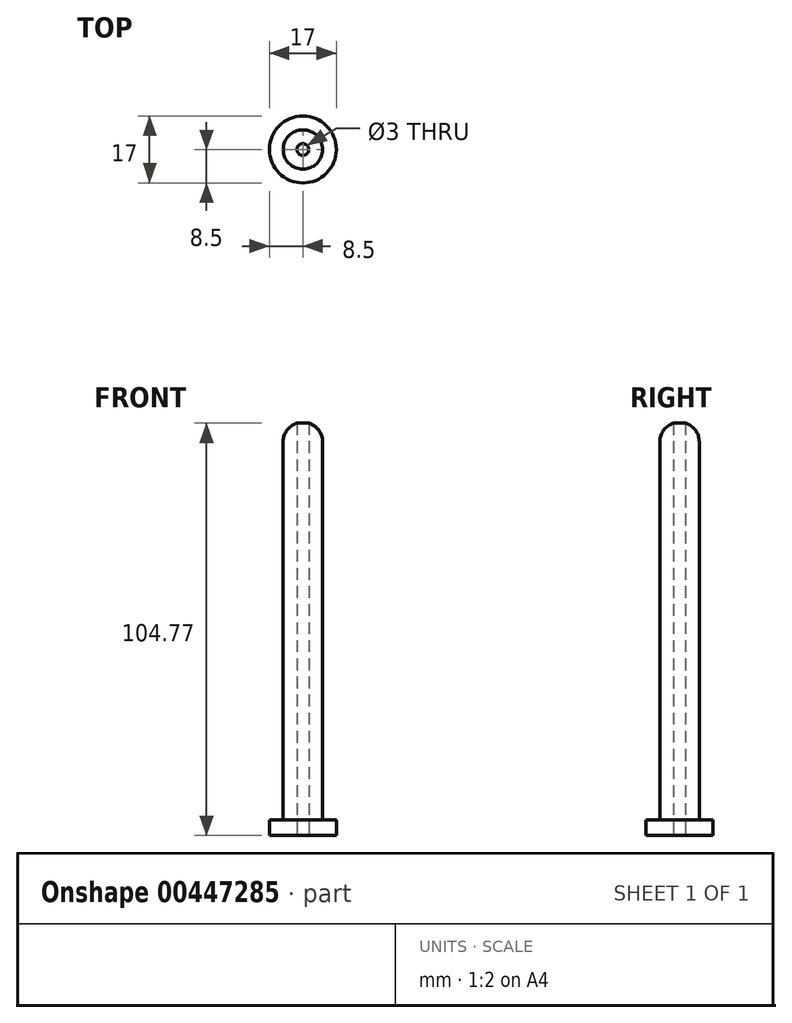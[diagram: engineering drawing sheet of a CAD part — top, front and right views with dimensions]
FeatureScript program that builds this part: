
annotation { "Feature Type Name" : "Feature", "Feature Type Description" : "" }
export const myFeature = defineFeature(function(context is Context, id is Id, definition is map)
    precondition{}
    {
        {
            var Q0;
            Q0=qCreatedBy(makeId("Top.planeOp"),FACE);
            var sketch = newSketch(context, id + "F0", { "sketchPlane" : qUnion([Q0])});
            skCircle(sketch, "E0", {"center": v(0, 0) * mm, "radius": 8.5 * mm});
            skSolve(sketch);
        }
        {
            var Q0;
            Q0=qSketchRegion(id+"F0",true);
            extrude(context, id + "F1", {"entities" : qUnion([Q0]), "depth" : 4 * mm});
        }
        {
            var Q0;
            Q0=qCreatedBy(makeId("Top.planeOp"),FACE);
            var sketch = newSketch(context, id + "F2", { "sketchPlane" : qUnion([Q0])});
            skCircle(sketch, "E1", {"center": v(0, 0) * mm, "radius": 5 * mm});
            skSolve(sketch);
        }
        {
            var Q0;
            Q0=qSketchRegion(id+"F2",true);
            extrude(context, id + "F3", {"entities" : qUnion([Q0]), "operationType" : NewBodyOperationType.ADD, "depth" : 100 * mm});
        }
        {
            var Q0;
            Q0=qCreatedBy(makeId("Right.planeOp"),FACE);
            var sketch = newSketch(context, id + "F4", { "sketchPlane" : qUnion([Q0])});
            skArc(sketch, "E2", {"start": v(5, 100) * mm, "mid": v(3.54, 103.54) * mm, "end": v(0, 105) * mm});
            skLineSegment(sketch, "E3", {"start": v(0, 105) * mm, "end": v(0, 100) * mm});
            skLineSegment(sketch, "E4", {"start": v(0, 100) * mm, "end": v(5, 100) * mm});
            skSolve(sketch);
        }
        {
            var Q0;
            Q0=qSketchRegion(id+"F4",true);
            var Q1;
            Q1=sQuery(id+"F4.wireOp",EDGE,"E3");
            revolve(context, id + "F5", {"operationType" : NewBodyOperationType.ADD, "entities" : qUnion([Q0]), "axis" : qUnion([Q1]), "revolveType" : RevolveType.FULL});
        }
        {
            var Q0;
            Q0=makeQuery(id+"F1.opExtrude","CAP_FACE",FACE,{"disambiguationData":[OSD([sQuery(id+"F0.wireOp",EDGE,"E0")])],"isStart":true});
            var sketch = newSketch(context, id + "F6", { "sketchPlane" : qUnion([Q0])});
            skCircle(sketch, "E5", {"center": v(0, 0) * mm, "radius": 1.5 * mm});
            skSolve(sketch);
        }
        {
            var Q0;
            Q0=makeQuery(id+"F6.imprint","IMPRINT",FACE,{"disambiguationData":[TD([[makeQuery(id+"F6.imprint","IMPRINT",EDGE,{"derivedFrom":sQuery(id+"F6.wireOp",EDGE,"E5")}),1.0]])]});
            extrude(context, id + "F7", {"entities" : qUnion([Q0]), "operationType" : NewBodyOperationType.REMOVE, "oppositeDirection" : true, "depth" : 133.7 * mm});
        }
    });
